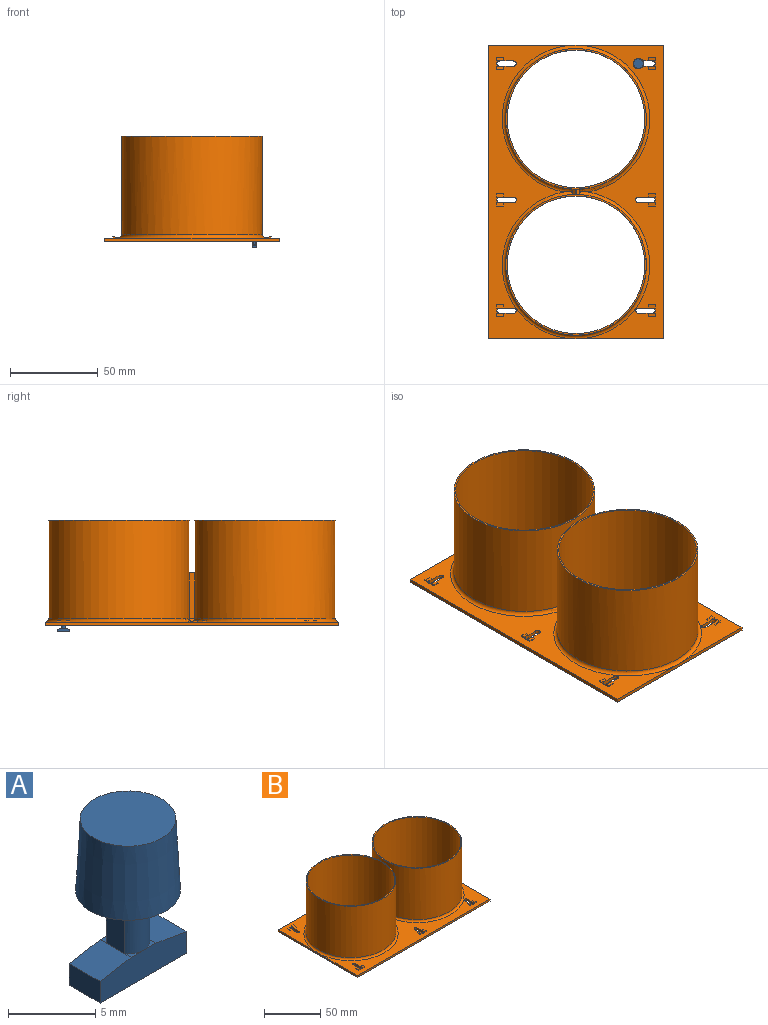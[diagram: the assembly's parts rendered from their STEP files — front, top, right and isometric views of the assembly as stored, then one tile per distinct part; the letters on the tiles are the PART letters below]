
ASSEMBLY  parts=2 mates=1
PART A: 18 faces, bbox 7x6x10.5 mm
  f0: plane 1x0.5mm, normal (0,0,1), area 0.2mm2, adj f4,f9,f14
  f1: plane 1x0.5mm, normal (0,0,1), area 0.2mm2, adj f8,f9,f14
  f2: plane 1x0.5mm, normal (0,0,1), area 0.2mm2, adj f8,f10,f12
  f3: plane 1x0.5mm, normal (0,0,1), area 0.2mm2, adj f4,f10,f12
  f4: plane 2.5x2.5mm, normal (-0.17,0,0.98), area 6.3mm2, adj f0,f3,f5,f9,f10,f13
  f5: plane 2.5x1.5mm, normal (-1,0,0), area 3.8mm2, adj f4,f6,f9,f10
  f6: plane 7x2.5mm, normal (0,0,-1), area 17.5mm2, adj f5,f7,f9,f10
  f7: plane 2.5x1.5mm, normal (1,0,0), area 3.8mm2, adj f6,f8,f9,f10
  f8: plane 2.5x2.5mm, normal (0.17,0,0.98), area 6.3mm2, adj f1,f2,f7,f9,f10,f11
  f9: plane 7x1.94mm, normal (0,-1,0), area 12.5mm2, adj f0,f1,f4,f5,f6,f7,f8
  f10: plane 7x1.94mm, normal (0,1,0), area 12.5mm2, adj f2,f3,f4,f5,f6,f7,f8
  f11: plane 3.6x1.5mm, normal (1,0,0), area 5.4mm2, adj f8,f12,f14,f17
  f12: cylinder r=1.25mm len=3.6mm, axis (0,0,-1), area 8.3mm2, adj f2,f3,f11,f13,f17
  f13: plane 3.6x1.5mm, normal (-1,0,0), area 5.4mm2, adj f4,f12,f14,f17
  f14: cylinder r=1.25mm len=3.6mm, axis (0,0,-1), area 8.3mm2, adj f0,f1,f11,f13,f17
  f15: cone r=3mm half-angle=3deg, axis (0,0,-1), area 90.3mm2, adj f16,f17
  f16: plane 5.48x5.48mm, normal (0,0,1), area 23.6mm2, adj f15
  f17: plane 6x6mm, normal (0,0,-1), area 23.9mm2, adj f11,f12,f13,f14,f15
PART B: 80 faces, bbox 177x100x60 mm
  f0: plane 167x50mm, normal (0,0,1), area 2671.3mm2, adj f5,f6,f7,f8,f9,f10,f11,f12
  f1: plane 167x50mm, normal (0,0,1), area 2671.3mm2, adj f2,f3,f4,f11,f13,f14,f15,f16
  f2: plane 9.5x2.9mm, normal (1,0,0), area 17.8mm2, adj f1,f3,f29,f30,f53,f54
  f3: cylinder r=1.5mm len=3mm, axis (0,0,-1), area 9.4mm2, adj f1,f2,f4,f30
  f4: plane 9.5x2.9mm, normal (-1,0,0), area 17.8mm2, adj f1,f3,f29,f30,f56,f57
  f5: cylinder r=1.5mm len=3mm, axis (0,0,-1), area 9.4mm2, adj f0,f6,f23,f30
  f6: plane 9.5x2.9mm, normal (1,0,0), area 17.8mm2, adj f0,f5,f7,f30,f59,f60
  f7: cylinder r=1.5mm len=3mm, axis (0,0,-1), area 9.4mm2, adj f0,f6,f23,f30
  f8: cylinder r=1.5mm len=3mm, axis (0,0,-1), area 9.4mm2, adj f0,f9,f24,f30
  f9: plane 9.5x2.9mm, normal (1,0,0), area 17.8mm2, adj f0,f8,f10,f30,f65,f66
  f10: cylinder r=1.5mm len=3mm, axis (0,0,-1), area 9.4mm2, adj f0,f9,f24,f30
  f11: plane 100x2mm, normal (1,0,0), area 200mm2, adj f0,f1,f12,f25,f30
  f12: plane 167x2mm, normal (0,1,0), area 334mm2, adj f0,f11,f13,f30
  f13: plane 100x2mm, normal (-1,0,0), area 200mm2, adj f0,f1,f12,f25,f30
  f14: plane 9.5x2.9mm, normal (1,0,0), area 17.8mm2, adj f1,f15,f26,f30,f47,f48
  f15: cylinder r=1.5mm len=3mm, axis (0,0,-1), area 9.4mm2, adj f1,f14,f16,f30
  f16: plane 9.5x2.9mm, normal (-1,0,0), area 17.8mm2, adj f1,f15,f26,f30,f50,f51
  f17: cylinder r=1.5mm len=3mm, axis (0,0,-1), area 9.4mm2, adj f0,f18,f27,f30
  f18: plane 9.5x2.9mm, normal (1,0,0), area 17.8mm2, adj f0,f17,f19,f30,f71,f72
  f19: cylinder r=1.5mm len=3mm, axis (0,0,-1), area 9.4mm2, adj f0,f18,f27,f30
  f20: plane 9.5x2.9mm, normal (-1,0,0), area 17.8mm2, adj f1,f21,f28,f30,f44,f45
  f21: cylinder r=1.5mm len=3mm, axis (0,0,-1), area 9.4mm2, adj f1,f20,f22,f30
  f22: plane 9.5x2.9mm, normal (1,0,0), area 17.8mm2, adj f1,f21,f28,f30,f41,f42
  f23: plane 9.5x2.9mm, normal (-1,0,0), area 17.8mm2, adj f0,f5,f7,f30,f62,f63
  f24: plane 9.5x2.9mm, normal (-1,0,0), area 17.8mm2, adj f0,f8,f10,f30,f68,f69
  f25: plane 167x2mm, normal (0,-1,0), area 334mm2, adj f1,f11,f13,f30
  f26: cylinder r=1.5mm len=3mm, axis (0,0,-1), area 9.4mm2, adj f1,f14,f16,f30
  f27: plane 9.5x2.9mm, normal (-1,0,0), area 17.8mm2, adj f0,f17,f19,f30,f74,f75
  f28: cylinder r=1.5mm len=3mm, axis (0,0,-1), area 9.4mm2, adj f1,f20,f22,f30
  f29: cylinder r=1.5mm len=3mm, axis (0,0,-1), area 9.4mm2, adj f1,f2,f4,f30
  f30: plane 167x100mm, normal (0,0,-1), area 6898mm2, adj f2,f3,f4,f5,f6,f7,f8,f9
  f31: cylinder r=40mm len=80mm, axis (0,0,-1), area 14051.5mm2, adj f33,f34,f37,f38,f78
  f32: cylinder r=40mm len=80mm, axis (0,0,-1), area 14051.5mm2, adj f33,f34,f37,f39,f79
  f33: plane 26x3.01mm, normal (0,-1,0), area 78.1mm2, adj f31,f32,f37,f77
  f34: plane 26x3.01mm, normal (0,1,0), area 78.1mm2, adj f31,f32,f37,f76
  f35: cylinder r=39.12mm len=78.24mm, axis (0,0,-1), area 14747.9mm2, adj f30,f38
  f36: cylinder r=39.12mm len=78.24mm, axis (0,0,-1), area 14747.9mm2, adj f30,f39
  f37: plane 3.01x0.88mm, normal (0,0,1), area 2.6mm2, adj f31,f32,f33,f34
  f38: plane 80x80mm, normal (0,0,1), area 218.7mm2, adj f31,f35
  f39: plane 80x80mm, normal (0,0,1), area 218.7mm2, adj f32,f36
  f40: plane 4x0.9mm, normal (-1,0,0), area 1.8mm2, adj f1,f41,f42
  f41: plane 2x0.9mm, normal (0,-1,0), area 1.8mm2, adj f1,f22,f40,f42
  f42: plane 4x2mm, normal (0,0.22,0.98), area 8.2mm2, adj f1,f22,f40,f41
  f43: plane 4x0.9mm, normal (1,0,0), area 1.8mm2, adj f1,f44,f45
  f44: plane 2x0.9mm, normal (0,-1,0), area 1.8mm2, adj f1,f20,f43,f45
  f45: plane 4x2mm, normal (0,0.22,0.98), area 8.2mm2, adj f1,f20,f43,f44
  f46: plane 4x0.9mm, normal (-1,0,0), area 1.8mm2, adj f1,f47,f48
  f47: plane 2x0.9mm, normal (0,-1,0), area 1.8mm2, adj f1,f14,f46,f48
  f48: plane 4x2mm, normal (0,0.22,0.98), area 8.2mm2, adj f1,f14,f46,f47
  f49: plane 4x0.9mm, normal (1,0,0), area 1.8mm2, adj f1,f50,f51
  f50: plane 2x0.9mm, normal (0,-1,0), area 1.8mm2, adj f1,f16,f49,f51
  f51: plane 4x2mm, normal (0,0.22,0.98), area 8.2mm2, adj f1,f16,f49,f50
  f52: plane 4x0.9mm, normal (-1,0,0), area 1.8mm2, adj f1,f53,f54
  f53: plane 2x0.9mm, normal (0,-1,0), area 1.8mm2, adj f1,f2,f52,f54
  f54: plane 4x2mm, normal (0,0.22,0.98), area 8.2mm2, adj f1,f2,f52,f53
  f55: plane 4x0.9mm, normal (1,0,0), area 1.8mm2, adj f1,f56,f57
  f56: plane 2x0.9mm, normal (0,-1,0), area 1.8mm2, adj f1,f4,f55,f57
  f57: plane 4x2mm, normal (0,0.22,0.98), area 8.2mm2, adj f1,f4,f55,f56
  f58: plane 4x0.9mm, normal (-1,0,0), area 1.8mm2, adj f0,f59,f60
  f59: plane 2x0.9mm, normal (0,1,0), area 1.8mm2, adj f0,f6,f58,f60
  f60: plane 4x2mm, normal (0,-0.22,0.98), area 8.2mm2, adj f0,f6,f58,f59
  f61: plane 4x0.9mm, normal (1,0,0), area 1.8mm2, adj f0,f62,f63
  f62: plane 2x0.9mm, normal (0,1,0), area 1.8mm2, adj f0,f23,f61,f63
  f63: plane 4x2mm, normal (0,-0.22,0.98), area 8.2mm2, adj f0,f23,f61,f62
  f64: plane 4x0.9mm, normal (-1,0,0), area 1.8mm2, adj f0,f65,f66
  f65: plane 2x0.9mm, normal (0,1,0), area 1.8mm2, adj f0,f9,f64,f66
  f66: plane 4x2mm, normal (0,-0.22,0.98), area 8.2mm2, adj f0,f9,f64,f65
  f67: plane 4x0.9mm, normal (1,0,0), area 1.8mm2, adj f0,f68,f69
  f68: plane 2x0.9mm, normal (0,1,0), area 1.8mm2, adj f0,f24,f67,f69
  f69: plane 4x2mm, normal (0,-0.22,0.98), area 8.2mm2, adj f0,f24,f67,f68
  f70: plane 4x0.9mm, normal (-1,0,0), area 1.8mm2, adj f0,f71,f72
  f71: plane 2x0.9mm, normal (0,1,0), area 1.8mm2, adj f0,f18,f70,f72
  f72: plane 4x2mm, normal (0,-0.22,0.98), area 8.2mm2, adj f0,f18,f70,f71
  f73: plane 4x0.9mm, normal (1,0,0), area 1.8mm2, adj f0,f74,f75
  f74: plane 2x0.9mm, normal (0,1,0), area 1.8mm2, adj f0,f27,f73,f75
  f75: plane 4x2mm, normal (0,-0.22,0.98), area 8.2mm2, adj f0,f27,f73,f74
  f76: plane 3.01x1.96mm, normal (0,0.71,0.71), area 6.2mm2, adj f34,f78,f79
  f77: plane 3.01x1.95mm, normal (0,-0.71,0.71), area 6.2mm2, adj f33,f78,f79
  f78: torus R=42mm, axis (0,0,1), area 791.1mm2, adj f0,f1,f31,f76,f77,f79
  f79: torus R=42mm, axis (0,0,1), area 791.1mm2, adj f0,f1,f32,f76,f77,f78
PLACE A rot(axis=(0,0,-1),89.5deg) t=(35.5,73,-2.57)mm
PLACE B rot(axis=(0,0,-1),90deg) t=(0,0,0)mm
MATE revolute A.f12 <-> B.f5  axis (0,0,-1) through (35.5,73,2)mm
